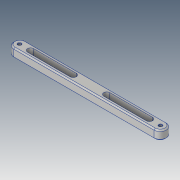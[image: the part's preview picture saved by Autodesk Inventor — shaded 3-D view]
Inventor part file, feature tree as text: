
AUTODESK INVENTOR PART (.ipt)
format: ipt  version: 2018.2 (Build 222227000, 227)  size: 137,216 bytes
history: native  units: mm
features: sketch x3, extrude x2, chamfer x2, mirror x1, fillet x1
ambient origin geometry x8: Origin, YZ Plane, XZ Plane, XY Plane, X Axis, Y Axis, Z Axis, Center Point
bodies: Volumenkörper1 (feature_tree)
feature tree (9):
  extrude  "Grundkörper"  Depth=20.0mm
  extrude  "Ausschnitt_Gewichtsreduktion"  Depth=15.0mm
  mirror  "Spiegeln_Ausschnitt_Gewichtsreduktion"
  chamfer  "Fase_M6_Gewinde"  Distance=0.5mm Angle=45.0deg
  fillet  "Abrundung"  Radius=10.0mm
  chamfer  "Fase2"  Distance=10.0mm
  sketch  "Skizze1"  dims[d0=250.0mm d1=20.0mm]
  sketch  "Skizze2"  dims[d2=15.0mm d3=0.0mm d4=231.2mm]
  sketch  "Skizze3"  dims[d5=4.917mm d6=12.0mm d7=6.0mm d8=2.0mm d9=90.0deg d10=17.1mm d11=20.594885mm d12=0.5mm d13=2.0mm d14=45.0deg d15=10.0mm d16=10.0mm d17=80.0mm d18=5.0mm d19=15.0mm d20=0.0mm d21=2.0mm d22=2.0mm d23=45.0deg]
